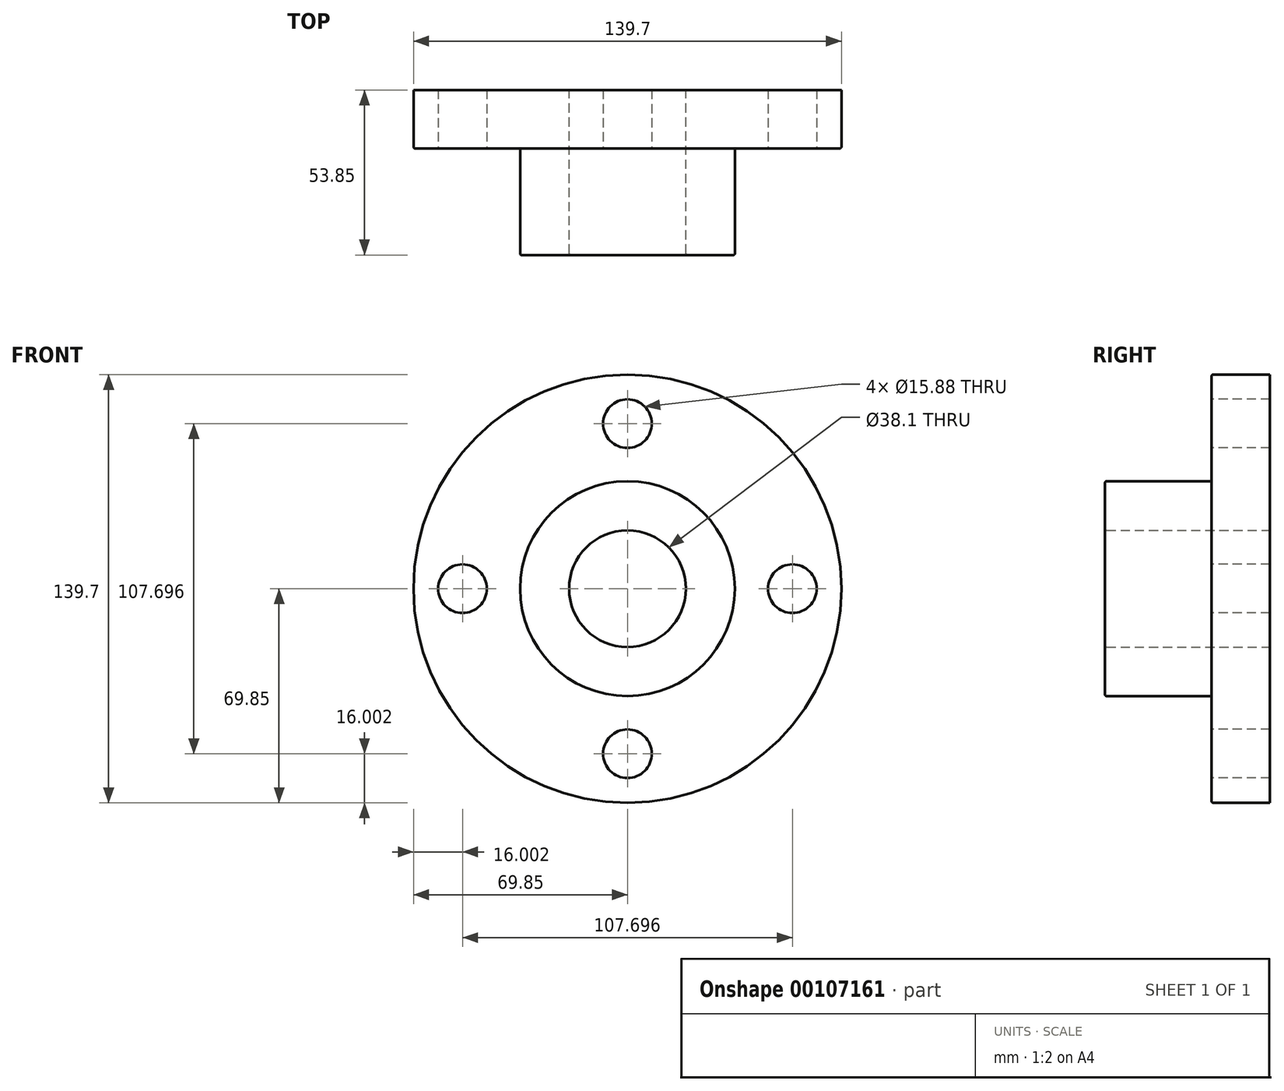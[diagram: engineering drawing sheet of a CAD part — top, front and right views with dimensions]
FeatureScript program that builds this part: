
annotation { "Feature Type Name" : "Feature", "Feature Type Description" : "" }
export const myFeature = defineFeature(function(context is Context, id is Id, definition is map)
    precondition{}
    {
        {
            var Q0;
            Q0=qCreatedBy(makeId("Right.planeOp"),FACE);
            var sketch = newSketch(context, id + "F0", { "sketchPlane" : qUnion([Q0])});
            skLineSegment(sketch, "E0", {"start": v(0, 0) * mm, "end": v(0, 35.05) * mm});
            skLineSegment(sketch, "E1", {"start": v(0, 35.05) * mm, "end": v(34.8, 35.05) * mm});
            skLineSegment(sketch, "E2", {"start": v(34.8, 35.05) * mm, "end": v(34.8, 69.85) * mm});
            skLineSegment(sketch, "E3", {"start": v(34.8, 69.85) * mm, "end": v(53.85, 69.85) * mm});
            skLineSegment(sketch, "E4", {"start": v(53.85, 69.85) * mm, "end": v(53.85, 0) * mm});
            skLineSegment(sketch, "E5", {"start": v(53.85, 0) * mm, "end": v(0, 0) * mm});
            skSolve(sketch);
        }
        {
            var Q0;
            Q0=makeQuery(id+"F0.imprint","IMPRINT",FACE,{"disambiguationData":[TD([[makeQuery(id+"F0.imprint","IMPRINT",EDGE,{"derivedFrom":sQuery(id+"F0.wireOp",EDGE,"E0")}),-1.0]])]});
            var Q1;
            Q1=sQuery(id+"F0.wireOp",EDGE,"E5");
            revolve(context, id + "F1", {"entities" : qUnion([Q0]), "axis" : qUnion([Q1]), "revolveType" : RevolveType.FULL});
        }
        {
            var Q0;
            Q0=makeQuery(id+"F1.opRevolve","SWEPT_FACE",FACE,{"disambiguationData":[OSD([sQuery(id+"F0.wireOp",EDGE,"E2")])]});
            var sketch = newSketch(context, id + "F2", { "sketchPlane" : qUnion([Q0])});
            skCircle(sketch, "E6", {"center": v(0, 0) * mm, "radius": 19.05 * mm});
            skSolve(sketch);
        }
        {
            var Q0;
            Q0 = qSketchRegion(id + "F2", true);
            extrude(context, id + "F3", {"entities" : qUnion([Q0]), "operationType" : NewBodyOperationType.REMOVE, "endBound" : BoundingType.SYMMETRIC, "depth" : 127 * mm});
        }
        {
            var Q0;
            Q0=makeQuery(id+"F1.opRevolve","SWEPT_FACE",FACE,{"disambiguationData":[OSD([sQuery(id+"F0.wireOp",EDGE,"E2")])]});
            var sketch = newSketch(context, id + "F4", { "sketchPlane" : qUnion([Q0])});
            skLineSegment(sketch, "E7", {"start": v(0, 0) * mm, "end": v(0, 53.85) * mm, "construction": true});
            skCircle(sketch, "E8", {"center": v(0, 53.85) * mm, "radius": 7.94 * mm});
            skCircle(sketch, "E9.1.0", {"center": v(-53.85, 0) * mm, "radius": 7.94 * mm});
            skCircle(sketch, "E9.2.0", {"center": v(0, -53.85) * mm, "radius": 7.94 * mm});
            skCircle(sketch, "E9.3.0", {"center": v(53.85, 0) * mm, "radius": 7.94 * mm});
            skPoint(sketch, "E9.center", {"position": v(0, 0) * mm});
            skSolve(sketch);
        }
        {
            var Q0;
            Q0 = qSketchRegion(id + "F4", true);
            var Q1;
            Q1=sQuery(id+"F4.wireOp",EDGE,"E8");
            var Q2;
            Q2=sQuery(id+"F4.wireOp",EDGE,"E9.1.0");
            var Q3;
            Q3=sQuery(id+"F4.wireOp",EDGE,"E9.2.0");
            var Q4;
            Q4=sQuery(id+"F4.wireOp",EDGE,"E9.3.0");
            extrude(context, id + "F5", {"entities" : qUnion([Q0]), "operationType" : NewBodyOperationType.REMOVE, "surfaceEntities" : qUnion([Q1, Q2, Q3, Q4]), "oppositeDirection" : true, "depth" : 127 * mm});
        }
        {
            var Q0;
            Q0 = qSketchRegion(id + "F4", true);
            extrude(context, id + "F6", {"entities" : qUnion([Q0]), "operationType" : NewBodyOperationType.REMOVE, "oppositeDirection" : true, "depth" : 25.4 * mm});
        }
        {
            var Q0;
            Q0=makeQuery(id+"F3.boolean.opBoolean","INTERSECT",EDGE,{"derivedFrom":[makeQuery(id+"F1.opRevolve","SWEPT_FACE",FACE,{"disambiguationData":[OSD([sQuery(id+"F0.wireOp",EDGE,"E0")])]}),makeQuery(id+"F3.opExtrude","SWEPT_FACE",FACE,{"disambiguationData":[OSD([sQuery(id+"F2.wireOp",EDGE,"E6")])]})]});
            fillet(context, id + "F7", {"entities" : qUnion([Q0]), "radius" : 0.5 * mm, "tangentPropagation" : true, "allowEdgeOverflow" : false});
        }
        {
            var Q0;
            Q0=makeQuery(id+"F1.opRevolve","SWEPT_EDGE",EDGE,{"disambiguationData":[OSD([sQuery(id+"F0.wireOp",EDGE,"E0"),sQuery(id+"F0.wireOp",EDGE,"E1")])]});
            var Q1;
            Q1=makeQuery(id+"F1.opRevolve","SWEPT_EDGE",EDGE,{"disambiguationData":[OSD([sQuery(id+"F0.wireOp",EDGE,"E1"),sQuery(id+"F0.wireOp",EDGE,"E2")])]});
            var Q2;
            Q2=makeQuery(id+"F1.opRevolve","SWEPT_EDGE",EDGE,{"disambiguationData":[OSD([sQuery(id+"F0.wireOp",EDGE,"E2"),sQuery(id+"F0.wireOp",EDGE,"E3")])]});
            fillet(context, id + "F8", {"entities" : qUnion([Q0, Q1, Q2]), "radius" : 0.5 * mm, "tangentPropagation" : true, "allowEdgeOverflow" : false});
        }
    });
